# Revit family: MRSF-D
name_source: partatom
category: Mechanical Equipment
units: mm (PartAtom-declared; Revit-internal decimal feet)

## family parameters
Always vertical = Yes
Cut with Voids When Loaded = No
Part Type = Normal
Room Calculation Point = No
Round Connector Dimension = Use Diameter
Shared = No
Work Plane-Based = No

## types (6) — shared parameters
0 = 0' - 0"
1" = 0' - 1"
1.5 = 0' - 1 1/2"
135 = 135.00°
2" = 0' - 2"
2' = 2' - 0"
3" = 0' - 3"
4" = 0' - 4"
8" = 0' - 8"
Manufacturer = Loren Cook Company
Model = MRSF-D
ONE EIGTH = 0' - 0 1/8"
Type Comments = Economizer Fan Mix, Recirculate, Supply - Filtered Direct Drive
URL = www.lorencook.com

## per-type parameters (varying)
- 24_MRSF-D: -(B/2)=-1' - 3 3/4"; -A=-5' - 0 1/4"; -A+3=-4' - 9 1/4"; -A+3.125"=-4' - 9 1/8"; -W/2=-2' - 10 1/2"; -W2/2=-2' - 10 1/2"; A=5' - 0 1/4"; A/2=2' - 6 1/8"; B=2' - 7 1/2"; B*.45=1' - 2 3/16"; B/2=1' - 3 3/4"; C=1' - 6"; C/2=0' - 9"; CURB_OD=2' - 11 1/2"; CURB_OD/2=1' - 5 3/4"; D=1' - 9 3/4"; E=1' - 11 3/4"; E/2=0' - 11 7/8"; H=2' - 2"; RO=2' - 8 1/2"; RO/2=1' - 4 1/4"; T_SQ=3' - 1 1/2"; T_SQ/2=1' - 6 3/4"; W=5' - 9"; W/2=2' - 10 1/2"; W2=5' - 9"; W2/2=2' - 10 1/2"
- 30_MRSF-D: -(B/2)=-1' - 6 3/4"; -A=-5' - 5 3/4"; -A+3=-5' - 2 3/4"; -A+3.125"=-5' - 2 5/8"; -W/2=-3' - 4"; -W2/2=-3' - 4"; A=5' - 5 3/4"; A/2=2' - 8 7/8"; B=3' - 1 1/2"; B*.45=1' - 4 7/8"; B/2=1' - 6 3/4"; C=1' - 6"; C/2=0' - 9"; CURB_OD=3' - 5 1/2"; CURB_OD/2=1' - 8 3/4"; D=2' - 3 1/4"; E=2' - 5 3/4"; E/2=1' - 2 7/8"; H=2' - 4"; RO=3' - 2 1/2"; RO/2=1' - 7 1/4"; T_SQ=3' - 7 1/2"; T_SQ/2=1' - 9 3/4"; W=6' - 8"; W/2=3' - 4"; W2=6' - 8"; W2/2=3' - 4"
- 36_MRSF-D: -(B/2)=-1' - 9 3/4"; -A=-5' - 11 1/4"; -A+3=-5' - 8 1/4"; -A+3.125"=-5' - 8 1/8"; -W/2=-3' - 9"; -W2/2=-3' - 9"; A=5' - 11 1/4"; A/2=2' - 11 5/8"; B=3' - 7 1/2"; B*.45=1' - 7 9/16"; B/2=1' - 9 3/4"; C=1' - 6"; C/2=0' - 9"; CURB_OD=3' - 11 1/2"; CURB_OD/2=1' - 11 3/4"; D=2' - 8 3/4"; E=2' - 11 3/4"; E/2=1' - 5 7/8"; H=2' - 5"; RO=3' - 8 1/2"; RO/2=1' - 10 1/4"; T_SQ=4' - 1 1/2"; T_SQ/2=2' - 0 3/4"; W=7' - 6"; W/2=3' - 9"; W2=7' - 6"; W2/2=3' - 9"
- 42_MRSF-D: -(B/2)=-2' - 0 3/4"; -A=-6' - 6 3/4"; -A+3=-6' - 3 3/4"; -A+3.125"=-6' - 3 5/8"; -W/2=-3' - 9"; -W2/2=-4' - 7"; A=6' - 6 3/4"; A/2=3' - 3 3/8"; B=4' - 1 1/2"; B*.45=1' - 10 9/32"; B/2=2' - 0 3/4"; C=1' - 8"; C/2=0' - 10"; CURB_OD=4' - 5 1/2"; CURB_OD/2=2' - 2 3/4"; D=3' - 2 1/4"; E=3' - 5 3/4"; E/2=1' - 8 7/8"; H=3' - 3"; RO=4' - 2 1/2"; RO/2=2' - 1 1/4"; T_SQ=4' - 7 1/2"; T_SQ/2=2' - 3 3/4"; W=7' - 6"; W/2=3' - 9"; W2=9' - 2"; W2/2=4' - 7"
- 48_MRSF-D: -(B/2)=-2' - 3 3/4"; -A=-7' - 0 1/4"; -A+3=-6' - 9 1/4"; -A+3.125"=-6' - 9 1/8"; -W/2=-4' - 6 1/2"; -W2/2=-4' - 6 1/2"; A=7' - 0 1/4"; A/2=3' - 6 1/8"; B=4' - 7 1/2"; B*.45=2' - 0 31/32"; B/2=2' - 3 3/4"; C=1' - 8"; C/2=0' - 10"; CURB_OD=4' - 11 1/2"; CURB_OD/2=2' - 5 3/4"; D=3' - 7 3/4"; E=3' - 11 3/4"; E/2=1' - 11 7/8"; H=3' - 3"; RO=4' - 8 1/2"; RO/2=2' - 4 1/4"; T_SQ=5' - 1 1/2"; T_SQ/2=2' - 6 3/4"; W=9' - 1"; W/2=4' - 6 1/2"; W2=9' - 1"; W2/2=4' - 6 1/2"
- 54_MRSF-D: -(B/2)=-2' - 6 3/4"; -A=-7' - 5 3/4"; -A+3=-7' - 2 3/4"; -A+3.125"=-7' - 2 5/8"; -W/2=-4' - 11 1/2"; -W2/2=-4' - 11 1/2"; A=7' - 5 3/4"; A/2=3' - 8 7/8"; B=5' - 1 1/2"; B*.45=2' - 3 11/16"; B/2=2' - 6 3/4"; C=1' - 8"; C/2=0' - 10"; CURB_OD=5' - 5 1/2"; CURB_OD/2=2' - 8 3/4"; D=4' - 1 1/4"; E=4' - 5 3/4"; E/2=2' - 2 7/8"; H=3' - 6"; RO=5' - 2 1/2"; RO/2=2' - 7 1/4"; T_SQ=5' - 7 1/2"; T_SQ/2=2' - 9 3/4"; W=9' - 11"; W/2=4' - 11 1/2"; W2=9' - 11"; W2/2=4' - 11 1/2"

## geometry (parser evidence)
native form markers: Sweep x2
no freeform markers — native parametric forms only
